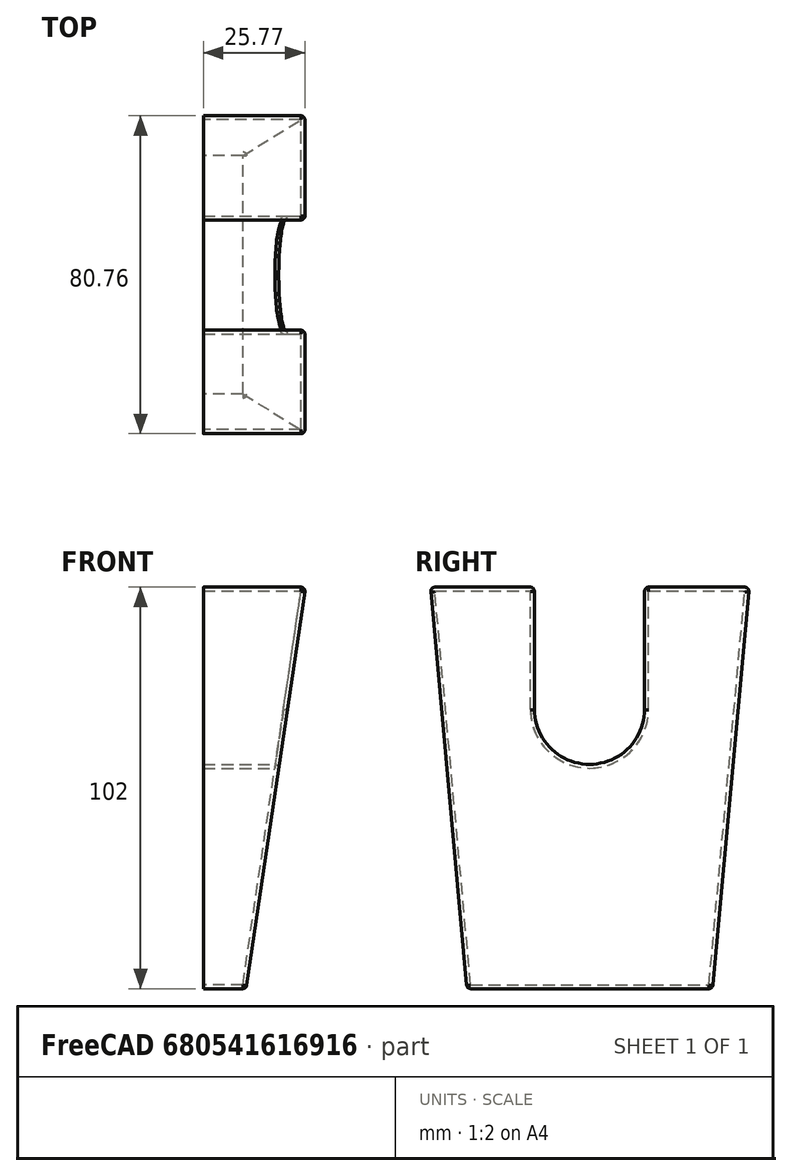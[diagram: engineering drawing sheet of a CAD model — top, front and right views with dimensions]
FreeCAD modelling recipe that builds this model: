
FCSTD DOCUMENT  (FreeCAD 0.14R3702 (Git))
Label: Claptrapfaceshell
License: CC-BY 3.0
LicenseURL: http://creativecommons.org/licenses/by/3.0/
objects: Part::Box×5, Part::Cut×4, Part::Cylinder×1, Part::MultiFuse×1, Part::Thickness×1
note: 12 computed .brp shape members not serialized (recipe doc carries the construction recipe); baked Part::Feature solids carry a one-line shape summary decoded from their .brp

FEATURE [Part::Box] Box  label="Cube"
  Height = 100
  Length = 25
  Width = 80
FEATURE [Part::Box] Box001  label="Cube001"
  Height = 110
  Length = 19
  Placement = pos=(10,0,0) rot=(0,1,0;0.146608rad)
  Width = 100
FEATURE [Part::Cut] Cut
  Base = -> Box
  Tool = -> Box001
FEATURE [Part::Box] Box003  label="Cube003"
  Height = 120
  Length = 40
  Placement = pos=(0,-30,-4) rot=(1,0,0;0.090757rad)
  Width = 40
FEATURE [Part::Box] Box004  label="Cube002"
  Height = 120
  Length = 40
  Placement = pos=(0,70,-4) rot=(-1,0,0;0.090757rad)
  Width = 40
FEATURE [Part::Cut] Cut001
  Base = -> Cut
  Tool = -> Box003
FEATURE [Part::Cut] Cut002
  Base = -> Cut001
  Tool = -> Box004
FEATURE [Part::Box] Box005  label="Cube004"
  Height = 30
  Length = 100
  Placement = pos=(0,25,70) rot=(0,0,1;0rad)
  Width = 30
FEATURE [Part::Cylinder] Cylinder
  Angle = 360
  Height = 100
  Placement = pos=(0,40,70) rot=(0,1,0;1.5708rad)
  Radius = 15
FEATURE [Part::MultiFuse] Fusion
  Shapes = -> [Box005,Cylinder]
FEATURE [Part::Cut] Cut003
  Base = -> Cut002
  Tool = -> Fusion
FEATURE [Part::Thickness] Thickness
  Faces = -> Cut003 [Face1]
  Intersection = false
  Join = 0
  Mode = 0
  SelfIntersection = false
  Value = 1
